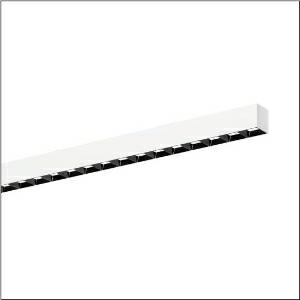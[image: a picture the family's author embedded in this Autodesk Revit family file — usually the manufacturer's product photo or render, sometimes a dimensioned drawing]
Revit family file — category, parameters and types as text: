
# Revit family: silica_21_51mx22tat4w
name_source: partatom
category: Lighting Fixtures
units: mm (PartAtom-declared; Revit-internal decimal feet)

## family parameters
Cut with Voids When Loaded = No
Host = Face
Light Source = No
Part Type = Normal
Room Calculation Point = No
Round Connector Dimension = Use Diameter
Shared = No

## types (1)
- --- (1 x LED, 3720 lm, 32.1 W, 6500K)
    Apparent Load = 32 VA
    CIE Flux Codes = 84 100 100 100 100
    Color Rendering = 80
    Color Temperature = 6500K
    Default Elevation = 1800 mm
    Description = Silica 21, office luminaire, primary light control with darklight reflector, of PMMA, black, CAT 2 (L<= 3000cd/m²), light emission: direct distribution, primary light characteristic: symmetric, installation type: surface-mounted, LED, rated luminous flux: 3.720lm, luminous efficacy: 110lm/W, light colour: 8tw, colour temperature: 2700..6500K, control gear: DALI DT8, with terminal, 3+2-pole, max. 2.5mm², mains connection: 220..240V, AC, 50/60Hz, rated input power: 33.8W, luminaire housing, of aluminium, traffic white (RAL 9016), length: 1.204mm, width: 53mm, height: 53mm, protection rating (complete): IP20, insulation class (complete): insulation class I (protective earthing), certification: CE, permissible operating ambient temperature: 0..+35°C, standard: EN 50419, packaging unit: 1 piece
    Height = 53 mm
    Lamp = 1 x LED
    Lamp Light Flux = 3720 lm
    Lamp Power = 32.1 W
    Lamp count = 1
    Length = 1204 mm
    Luminous efficacy = 116 lm/W
    Manufacturer = Siteco
    ModVariant = No
    Model = 51MX22TAT4W
    Mounting Place = Ceiling
    Mounting Type = Surface mounted
    Number of Poles = 1
    OnlyDefault = Yes
    Power Factor = 1
    Product Name = Silica 21
    Product group = office luminaire | ceiling mounted
    ProductGroupID = 301
    Protection Class = Protection class I
    Protection Degree = IP 20
    RLX_Detail_Level = 1
    RLX_Emergency_Light_Flux = 0 lm
    RLX_Emergency_Type = 0
    RLX_Emergency_Type_DB = No
    RlxData = <blob elided: 37949 chars, md5=be5cf07d>
    Socket = socket
    Standby Power = 0 W
    System Light Flux = 3720 lm
    System Power = 32 W
    Type Comments = individual setting
    Type Image = l_1335873.jpg
    URL = http://relux.com
    VarID = @adj_139655
    Voltage = 0 V
    Weight = 0.00 kg
    Width = 53 mm

## geometry (parser evidence)
native form markers: Blend x4, Sweep x11
no freeform markers — native parametric forms only
